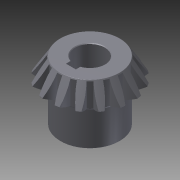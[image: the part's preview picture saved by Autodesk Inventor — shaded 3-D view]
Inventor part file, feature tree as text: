
AUTODESK INVENTOR PART (.ipt)
format: ipt  version: 2012 (Build 160160000, 160)  size: 295,936 bytes
history: native  units: in
note: dims shown in document units (in); Inventor stores cm internally (conversion verified against a paired STEP export)
features: other x1, extrude x1, imported_body x1, sketch x1
ambient origin geometry x8: Origin, YZ Plane, XZ Plane, XY Plane, X Axis, Y Axis, Z Axis, Center Point
bodies: Solid1 (feature_tree)
feature tree (4):
  other  "GE_110_6_0.sat1"
  extrude  "Extrusion1"  Depth=0.0625in
  imported_body  "Base1"
  sketch  "Sketch1"  dims[d1=0.125in d2=0.0625in d3=0.125in d4=0.3937in d5=0.0in]
